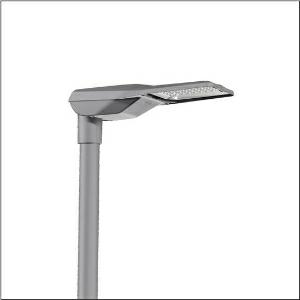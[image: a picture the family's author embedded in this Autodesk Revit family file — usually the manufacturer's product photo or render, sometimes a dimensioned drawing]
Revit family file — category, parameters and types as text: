
# Revit family: streetlight_sl_21_mini___st1_0a_5xe6d33a08gb_d47e
name_source: partatom
category: Lighting Fixtures
units: mm (PartAtom-declared; Revit-internal decimal feet)

## family parameters
Cut with Voids When Loaded = No
Host = Face
Light Source = No
Part Type = Normal
Room Calculation Point = No
Round Connector Dimension = Use Diameter
Shared = No

## types (1)
- --- (1 x LED, 5940 lm, 40.4 W, 3000K)
    Apparent Load = 40 VA
    CIE Flux Codes = 37 72 97 100 100
    Color Rendering = 70
    Color Temperature = 3000K
    Default Elevation = 1800 mm
    Description = Streetlight SL 21 mini, mast luminaire, primary light control with lens, of PMMA, primary optical cover: cover, of toughened safety glass, transparent, light distribution: ST1.0a, light emission: direct distribution, primary light characteristic: asymmetric, installation type: post-top, side-entry, LED, 3G 1.5mm², High Power LED, rated luminous flux: 5.940lm, luminous efficacy: 147lm/W, light colour: 730, colour temperature: 3000K, control gear: Easy, control: flexible luminous flux parameterisation, time-dependent luminous flux control, constant luminous flux control, overheat protection, mains connection: 230..240V, AC, 50/60Hz, connection cable pre-assembled, cable length: 6,5m, wiring characteristics: H07RN-F, start of lifetime: 40W, end of service life: 41W, reduction: 19W, luminaire housing, of diecast aluminium, powder-coated, Siteco® metallic grey (DB 702S), corrosivity category C5 mid according to DIN EN ISO 12944, please order mast flange separately, inclination adjustable: 0°, 5°, 10°, 15°, sealing non-destructively replaceable, multi-level sealing system, length: 628mm, width: 235mm, height: 110mm, mast flange for spigot size: 42mm (side-entry): 5XC10008XM4, 60/48mm (side-entry/post-top): 5XC10108XM2, 76/60mm (side-entry/post-top): 5XC10108XM1, mounting height: 4..8m, protection rating (complete): IP66, insulation class (complete): insulation class II (safety insulation), certification: CE, ENEC, ENEC+, VDE, impact resistance: IK10, permissible operating ambient temperature for outdoor applications: -40..+50°C, standard-compliant lighting for roads and squares, packaging unit: 1 piece

Light Distribution: ST1.0a
    Height = 110 mm
    Lamp = 1 x LED
    Lamp Light Flux = 5940 lm
    Lamp Power = 40.4 W
    Lamp count = 1
    Length = 625 mm
    Luminous efficacy = 147 lm/W
    Manufacturer = Siteco
    ModVariant = No
    Model = 5XE6D33A08GB
    Number of Poles = 1
    OnlyDefault = Yes
    Power Factor = 1
    Product Name = Streetlight SL 21 mini | ST1.0a
    Product group = mast luminaire | pylon top
    ProductGroupID = 6100
    Protection Class = Protection class II
    Protection Degree = IP 66
    RLX_Detail_Level = 1
    RLX_Emergency_Light_Flux = 0 lm
    RLX_Emergency_Type = 0
    RLX_Emergency_Type_DB = No
    RlxData = <blob elided: 25937 chars, md5=e65b3bfb>
    Socket = socket
    Standby Power = 0 W
    System Light Flux = 5940 lm
    System Power = 40 W
    Type Comments = factory setting: luminous flux: 100 % | Output Level: 100 % | 812 mA
    Type Image = l_1003519.jpg
    URL = http://relux.com
    VarID = @adj_188362
    Voltage = 0 V
    Weight = 0.00 kg
    Width = 234 mm

## geometry (parser evidence)
native form markers: Blend x4, Sweep x11
no freeform markers — native parametric forms only
